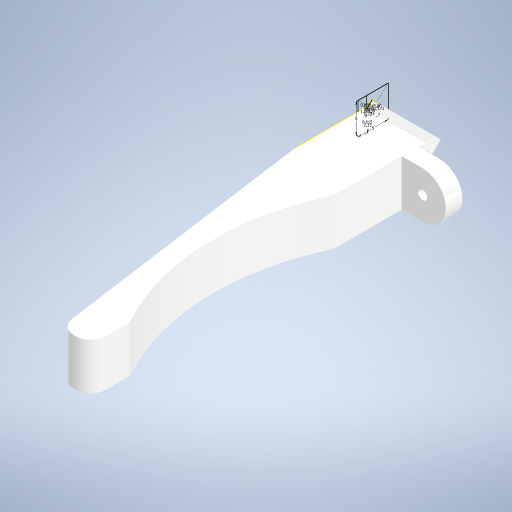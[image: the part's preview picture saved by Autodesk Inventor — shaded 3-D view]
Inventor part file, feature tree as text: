
AUTODESK INVENTOR PART (.ipt)
format: ipt  version: 2024 (Build 280153000, 153)  size: 337,920 bytes
history: native  units: in
note: dims shown in document units (in); Inventor stores cm internally (conversion verified against a paired STEP export)
features: extrude x4, sketch x2, other x1, plane x1, mirror x1, projected_geometry x1, fillet x1
ambient origin geometry x8: Origin, YZ Plane, XZ Plane, XY Plane, X Axis, Y Axis, Z Axis, Center Point
bodies: Solid1 (feature_tree)
feature tree (11):
  other  "Plane1"
  sketch  "Sketch1"  dims[d10=0.0787in d11=0.0787in]
  extrude  "Extrusion1"  Depth=0.0787in
  extrude  "Extrusion2"  Depth=0.3937in
  plane  "Work Plane2"
  extrude  "Extrusion3"  TaperAngle=0.0deg  [1 undecoded]
  extrude  "Extrusion4"  TaperAngle=0.0deg  [1 undecoded]
  mirror  "Mirror1"
  projected_geometry  "Projected Loop1"
  sketch  "Sketch2"  dims[d12=45.0deg d13=0.0414in d14=0.0in d15=0.0in d16=0.035in d17=0.0461in d18=0.0242in d19=0.0108in d20=0.035in d21=0.1969in d22=0.1969in d23=0.0134in d24=0.0423in d25=0.0in d26=0.0in d27=0.3937in d28=0.0in d29=0.0846in d30=0.0846in d31=0.3937in d32=0.0in d33=0.0394in d34=0.0394in d35=0.0in d36=0.0in]
  fillet  "Fillet1"  Radius=0.035in
note: 2 required parameter values undecoded (feature->parameter linkage not recoverable at this tier; creation-order binding heuristic only, values carry confidence <= 0.55)
